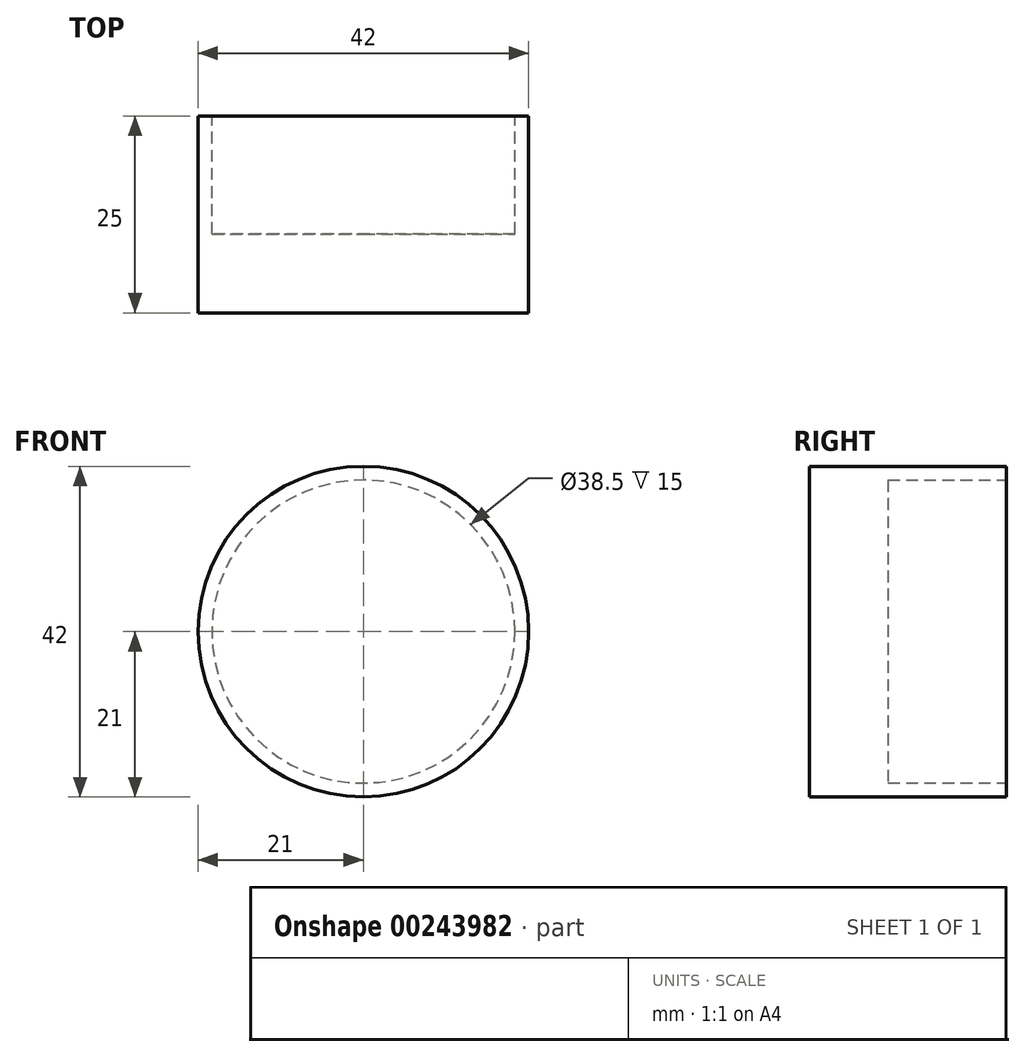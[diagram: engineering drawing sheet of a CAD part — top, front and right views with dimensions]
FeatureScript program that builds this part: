
annotation { "Feature Type Name" : "Feature", "Feature Type Description" : "" }
export const myFeature = defineFeature(function(context is Context, id is Id, definition is map)
    precondition{}
    {
        {
            var Q0;
            Q0=qCreatedBy(makeId("Front.planeOp"),FACE);
            var sketch = newSketch(context, id + "F0", { "sketchPlane" : qUnion([Q0])});
            skCircle(sketch, "E0", {"center": v(0, 0) * mm, "radius": 21 * mm});
            skSolve(sketch);
        }
        {
            var Q0;
            Q0=qSketchRegion(id+"F0",true);
            extrude(context, id + "F1", {"entities" : qUnion([Q0]), "oppositeDirection" : true, "depth" : 25 * mm});
        }
        {
            var Q0;
            Q0=makeQuery(id+"F1.opExtrude","CAP_FACE",FACE,{"disambiguationData":[OSD([sQuery(id+"F0.wireOp",EDGE,"E0")])],"isStart":false});
            var sketch = newSketch(context, id + "F2", { "sketchPlane" : qUnion([Q0])});
            skCircle(sketch, "E1", {"center": v(0, 0) * mm, "radius": 19.25 * mm});
            skSolve(sketch);
        }
        {
            var Q0;
            Q0 = qSketchRegion(id + "F2", true);
            extrude(context, id + "F3", {"entities" : qUnion([Q0]), "operationType" : NewBodyOperationType.REMOVE, "oppositeDirection" : true, "depth" : 15 * mm, "offsetDistance" : 25 * mm});
        }
    });
